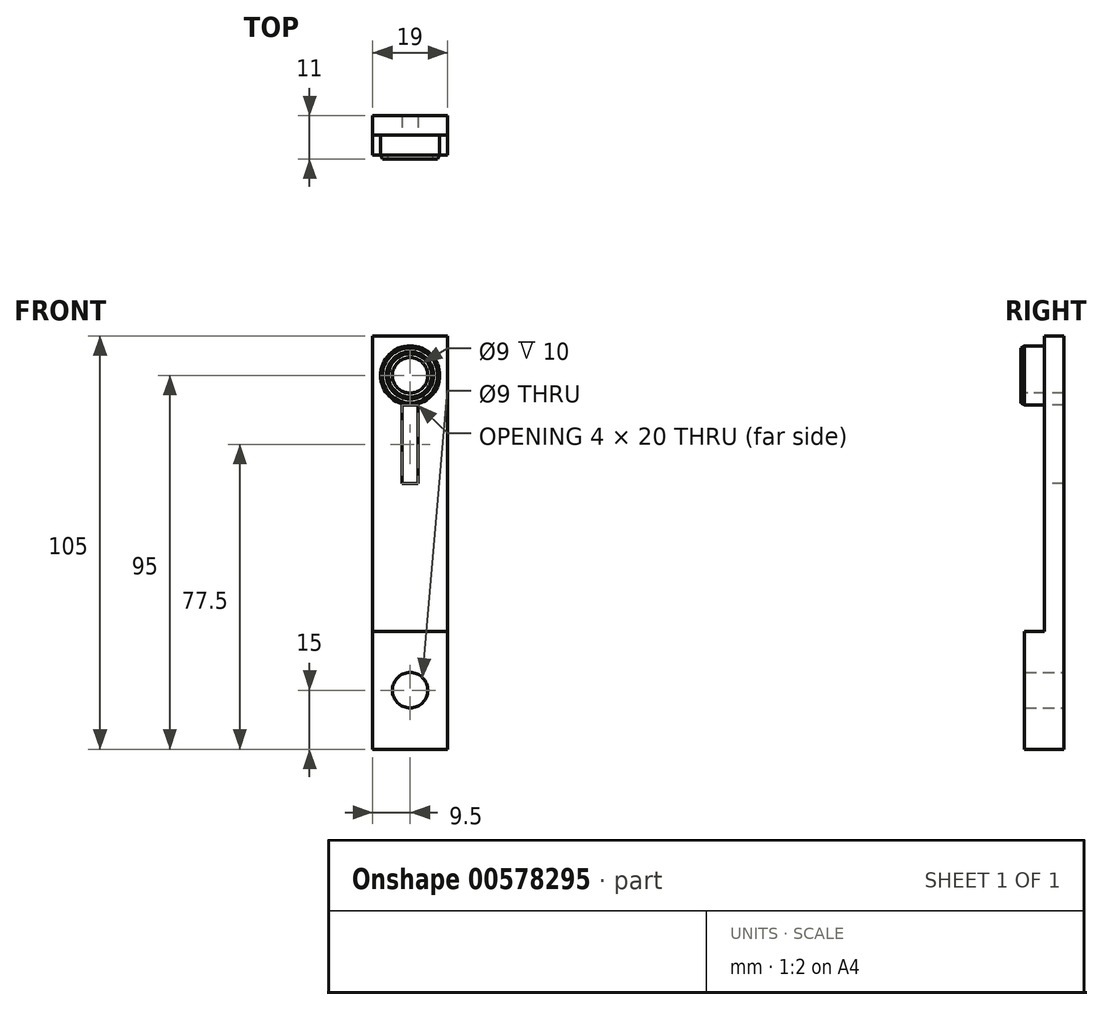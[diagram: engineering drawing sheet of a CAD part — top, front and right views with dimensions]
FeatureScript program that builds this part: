
annotation { "Feature Type Name" : "Feature", "Feature Type Description" : "" }
export const myFeature = defineFeature(function(context is Context, id is Id, definition is map)
    precondition{}
    {
        {
            var Q0;
            Q0=qCreatedBy(makeId("Front.planeOp"),FACE);
            var sketch = newSketch(context, id + "F0", { "sketchPlane" : qUnion([Q0])});
            skLineSegment(sketch, "E0.bottom", {"start": v(9.5, 10) * mm, "end": v(-9.5, 10) * mm});
            skLineSegment(sketch, "E0.top", {"start": v(9.5, -95) * mm, "end": v(-9.5, -95) * mm});
            skLineSegment(sketch, "E0.left", {"start": v(9.5, 10) * mm, "end": v(9.5, -95) * mm});
            skLineSegment(sketch, "E0.right", {"start": v(-9.5, 10) * mm, "end": v(-9.5, -95) * mm});
            skPoint(sketch, "E0.middle", {"position": v(0, -42.5) * mm});
            skPoint(sketch, "E1", {"position": v(0, -80) * mm});
            skSolve(sketch);
        }
        {
            var Q0;
            Q0 = qSketchRegion(id + "F0", true);
            extrude(context, id + "F1", {"entities" : qUnion([Q0]), "depth" : 5 * mm, "offsetDistance" : 25 * mm});
        }
        {
            var Q0;
            Q0=makeQuery(id+"F1.opExtrude","CAP_FACE",FACE,{"disambiguationData":[OSD([sQuery(id+"F0.wireOp",EDGE,"E0.bottom"),sQuery(id+"F0.wireOp",EDGE,"E0.top"),sQuery(id+"F0.wireOp",EDGE,"E0.left"),sQuery(id+"F0.wireOp",EDGE,"E0.right")])],"isStart":false});
            var sketch = newSketch(context, id + "F2", { "sketchPlane" : qUnion([Q0])});
            skCircle(sketch, "E2", {"center": v(0, 0) * mm, "radius": 7.5 * mm});
            skSolve(sketch);
        }
        {
            var Q0;
            Q0 = qSketchRegion(id + "F2", true);
            extrude(context, id + "F3", {"entities" : qUnion([Q0]), "operationType" : NewBodyOperationType.ADD, "depth" : 5 * mm, "offsetDistance" : 25 * mm});
        }
        {
            var Q0;
            Q0=qCreatedBy(makeId("Right.planeOp"),FACE);
            var sketch = newSketch(context, id + "F4", { "sketchPlane" : qUnion([Q0])});
            skLineSegment(sketch, "E3", {"start": v(-10, 7.5) * mm, "end": v(-11, 7) * mm});
            skLineSegment(sketch, "E4", {"start": v(-11, 7) * mm, "end": v(-11, 6) * mm});
            skLineSegment(sketch, "E5", {"start": v(-11, 6) * mm, "end": v(-10, 5.5) * mm});
            skLineSegment(sketch, "E6", {"start": v(-10, 5.5) * mm, "end": v(-10, 7.5) * mm});
            skPoint(sketch, "E7", {"position": v(-11, 6.5) * mm});
            skPoint(sketch, "E8", {"position": v(-10, 6.5) * mm});
            skLineSegment(sketch, "E9", {"start": v(-11, 0) * mm, "end": v(-10, 0) * mm});
            skSolve(sketch);
        }
        {
            var Q0;
            Q0 = qSketchRegion(id + "F4", true);
            var Q1;
            Q1=sQuery(id+"F4.wireOp",EDGE,"E9");
            revolve(context, id + "F5", {"operationType" : NewBodyOperationType.ADD, "entities" : qUnion([Q0]), "axis" : qUnion([Q1]), "revolveType" : RevolveType.FULL});
        }
        {
            var Q0;
            Q0=makeQuery(id+"F3.opExtrude","CAP_FACE",FACE,{"disambiguationData":[OSD([sQuery(id+"F2.wireOp",EDGE,"E2")])],"isStart":false});
            var sketch = newSketch(context, id + "F6", { "sketchPlane" : qUnion([Q0])});
            skCircle(sketch, "E10", {"center": v(0, 0) * mm, "radius": 4.5 * mm});
            skSolve(sketch);
        }
        {
            var Q0;
            Q0 = qSketchRegion(id + "F6", true);
            extrude(context, id + "F7", {"entities" : qUnion([Q0]), "operationType" : NewBodyOperationType.REMOVE, "endBound" : BoundingType.THROUGH_ALL, "oppositeDirection" : true, "depth" : 25 * mm, "offsetDistance" : 25 * mm});
        }
        {
            var Q0;
            Q0=makeQuery(id+"F1.opExtrude","CAP_FACE",FACE,{"disambiguationData":[OSD([sQuery(id+"F0.wireOp",EDGE,"E0.bottom"),sQuery(id+"F0.wireOp",EDGE,"E0.top"),sQuery(id+"F0.wireOp",EDGE,"E0.left"),sQuery(id+"F0.wireOp",EDGE,"E0.right")])],"isStart":true});
            var sketch = newSketch(context, id + "F8", { "sketchPlane" : qUnion([Q0])});
            skLineSegment(sketch, "E11.bottom", {"start": v(-9.5, -95) * mm, "end": v(9.5, -95) * mm});
            skLineSegment(sketch, "E11.top", {"start": v(-9.5, -65) * mm, "end": v(9.5, -65) * mm});
            skLineSegment(sketch, "E11.left", {"start": v(-9.5, -95) * mm, "end": v(-9.5, -65) * mm});
            skLineSegment(sketch, "E11.right", {"start": v(9.5, -95) * mm, "end": v(9.5, -65) * mm});
            skPoint(sketch, "E11.middle", {"position": v(0, -80) * mm});
            skSolve(sketch);
        }
        {
            var Q0;
            Q0 = qSketchRegion(id + "F8", true);
            extrude(context, id + "F9", {"entities" : qUnion([Q0]), "operationType" : NewBodyOperationType.ADD, "oppositeDirection" : true, "depth" : 10 * mm, "offsetDistance" : 25 * mm});
        }
        {
            var Q0;
            Q0=makeQuery(id+"F0.imprint","IMPRINT",FACE,{"disambiguationData":[TD([[makeQuery(id+"F0.imprint","IMPRINT",EDGE,{"derivedFrom":sQuery(id+"F0.wireOp",EDGE,"E0.bottom")}),1.0]])]});
            var sketch = newSketch(context, id + "F10", { "sketchPlane" : qUnion([Q0])});
            skCircle(sketch, "E12", {"center": v(0, -80) * mm, "radius": 4.5 * mm});
            skSolve(sketch);
        }
        {
            var Q0;
            Q0 = qSketchRegion(id + "F10", true);
            extrude(context, id + "F11", {"entities" : qUnion([Q0]), "operationType" : NewBodyOperationType.REMOVE, "endBound" : BoundingType.THROUGH_ALL, "depth" : 25 * mm, "offsetDistance" : 25 * mm});
        }
        {
            var Q0;
            Q0=makeQuery(id+"F1.opExtrude","CAP_FACE",FACE,{"disambiguationData":[OSD([sQuery(id+"F0.wireOp",EDGE,"E0.bottom"),sQuery(id+"F0.wireOp",EDGE,"E0.top"),sQuery(id+"F0.wireOp",EDGE,"E0.left"),sQuery(id+"F0.wireOp",EDGE,"E0.right")])],"isStart":false});
            var sketch = newSketch(context, id + "F12", { "sketchPlane" : qUnion([Q0])});
            skLineSegment(sketch, "E13.bottom", {"start": v(2, -7.5) * mm, "end": v(-2, -7.5) * mm});
            skLineSegment(sketch, "E13.top", {"start": v(2, -27.5) * mm, "end": v(-2, -27.5) * mm});
            skLineSegment(sketch, "E13.left", {"start": v(2, -7.5) * mm, "end": v(2, -27.5) * mm});
            skLineSegment(sketch, "E13.right", {"start": v(-2, -7.5) * mm, "end": v(-2, -27.5) * mm});
            skPoint(sketch, "E13.middle", {"position": v(0, -17.5) * mm});
            skSolve(sketch);
        }
        {
            var Q0;
            Q0 = qSketchRegion(id + "F12", true);
            extrude(context, id + "F13", {"entities" : qUnion([Q0]), "operationType" : NewBodyOperationType.REMOVE, "endBound" : BoundingType.UP_TO_NEXT, "oppositeDirection" : true, "depth" : 25 * mm, "offsetDistance" : 25 * mm});
        }
    });
